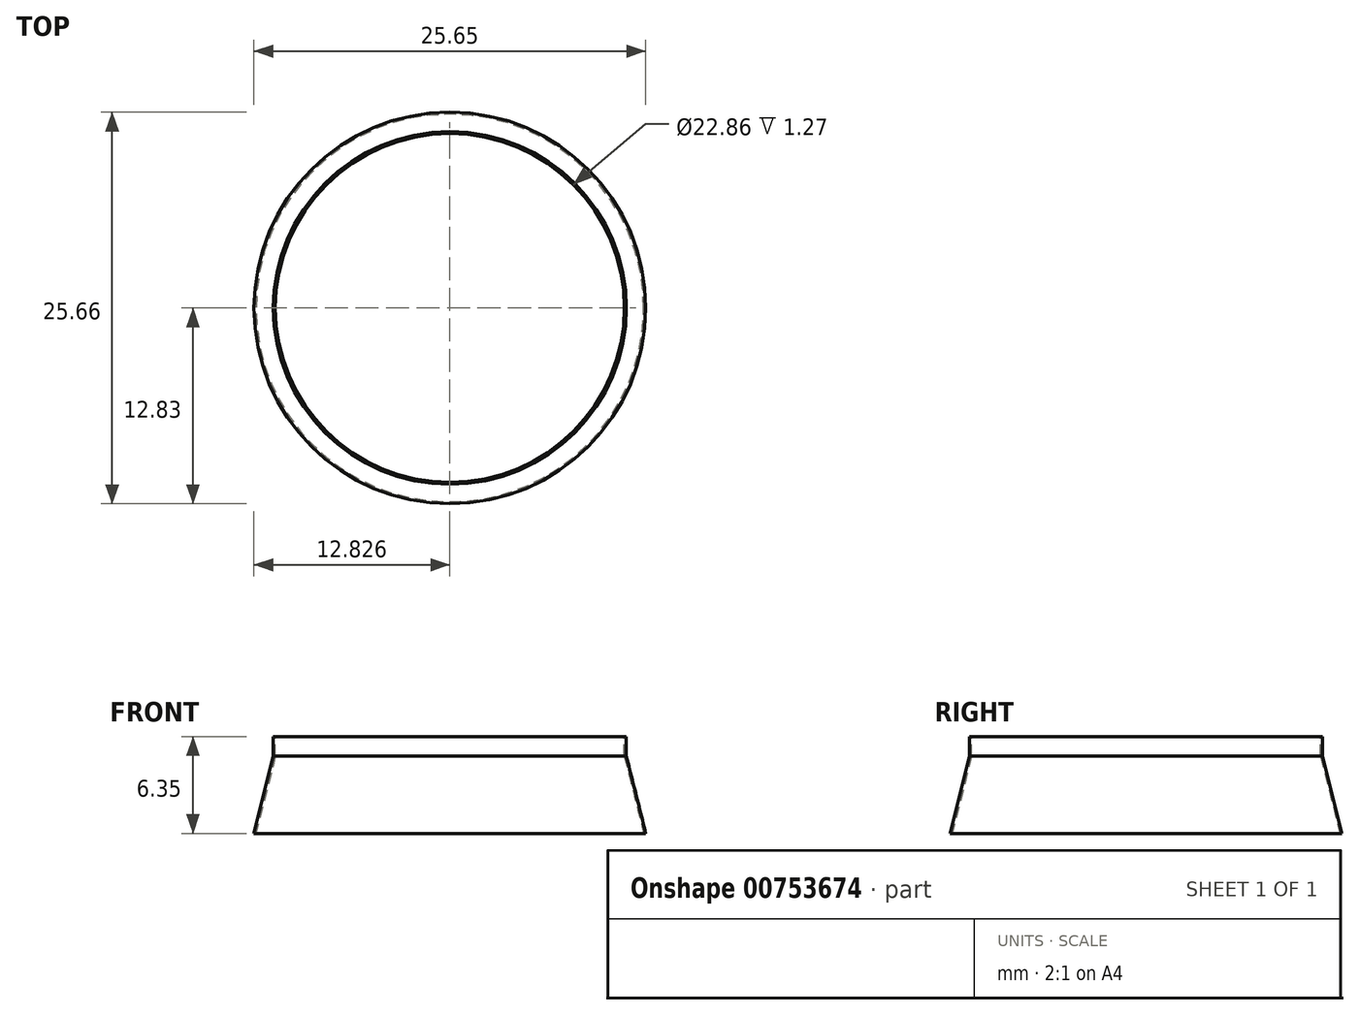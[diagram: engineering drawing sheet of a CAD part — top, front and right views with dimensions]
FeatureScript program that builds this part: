
annotation { "Feature Type Name" : "Feature", "Feature Type Description" : "" }
export const myFeature = defineFeature(function(context is Context, id is Id, definition is map)
    precondition{}
    {
        {
            var Q0;
            Q0=qCreatedBy(makeId("Front.planeOp"),FACE);
            var sketch = newSketch(context, id + "F0", { "sketchPlane" : qUnion([Q0])});
            skLineSegment(sketch, "E0", {"start": v(-10.65, 28.96) * mm, "end": v(-9.38, 23.88) * mm});
            skLineSegment(sketch, "E1", {"start": v(-10.65, 28.96) * mm, "end": v(-22.08, 28.96) * mm});
            skLineSegment(sketch, "E2", {"start": v(-9.38, 23.88) * mm, "end": v(-22.08, 23.88) * mm});
            skLineSegment(sketch, "E3", {"start": v(-22.08, 23.88) * mm, "end": v(-22.08, 28.96) * mm});
            skLineSegment(sketch, "E4", {"start": v(-10.65, 28.96) * mm, "end": v(-10.53, 28.96) * mm});
            skLineSegment(sketch, "E5", {"start": v(-9.38, 23.88) * mm, "end": v(-9.26, 23.88) * mm});
            skLineSegment(sketch, "E6", {"start": v(-10.53, 28.96) * mm, "end": v(-9.26, 23.88) * mm});
            skLineSegment(sketch, "E7", {"start": v(-10.53, 28.96) * mm, "end": v(-10.53, 30.23) * mm});
            skLineSegment(sketch, "E8", {"start": v(-10.53, 30.23) * mm, "end": v(-22.08, 30.23) * mm});
            skLineSegment(sketch, "E9", {"start": v(-22.08, 30.23) * mm, "end": v(-22.08, 28.96) * mm});
            skLineSegment(sketch, "E10", {"start": v(-10.65, 28.96) * mm, "end": v(-10.65, 30.23) * mm});
            skLineSegment(sketch, "E11", {"start": v(-10.65, 30.23) * mm, "end": v(-10.53, 30.23) * mm});
            skSolve(sketch);
        }
        {
            var Q0;
            Q0=makeQuery(id+"F0.imprint","IMPRINT",FACE,{"disambiguationData":[TD([[makeQuery(id+"F0.imprint","IMPRINT",EDGE,{"derivedFrom":sQuery(id+"F0.wireOp",EDGE,"E0")}),1.0]])]});
            var Q1;
            Q1=makeQuery(id+"F0.imprint","IMPRINT",FACE,{"disambiguationData":[TD([[makeQuery(id+"F0.imprint","IMPRINT",EDGE,{"derivedFrom":sQuery(id+"F0.wireOp",EDGE,"E4")}),1.0]])]});
            var Q2;
            Q2=sQuery(id+"F0.wireOp",EDGE,"E9");
            revolve(context, id + "F1", {"surfaceOperationType" : NewSurfaceOperationType.NEW, "entities" : qUnion([Q0, Q1]), "axis" : qUnion([Q2]), "revolveType" : RevolveType.FULL});
        }
    });
